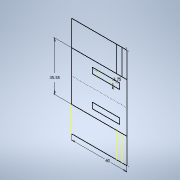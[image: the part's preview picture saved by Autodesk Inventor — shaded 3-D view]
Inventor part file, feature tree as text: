
AUTODESK INVENTOR PART (.ipt)
format: ipt  version: 2022 (Build 260153070, 153G)  size: 130,560 bytes
history: native  units: mm
features: other x7, reference x5, extrude x2, sketch x1, plane x1
ambient origin geometry x8: Origin, YZ Plane, XZ Plane, XY Plane, X Axis, Y Axis, Z Axis, Center Point
bodies: Solid1 (feature_tree)
feature tree (16):
  sketch  "Sketch1"  dims[d1=35.55mm d2=1.0mm d3=3.75mm d4=40.0mm d5=2.75mm d6=0.0mm d7=2.75mm d8=0.0mm]
  extrude  "Extrusion1"  Depth=2.75mm
  plane  "Work Plane1"
  extrude  "Extrusion2"  Depth=2.75mm
  reference  "Reference1"
  reference  "Reference2"
  reference  "Reference4"
  reference  "Reference5"
  reference  "Reference6"
  other  "<userpath> laptop\Desktop\SumoBot\FullBot.iam"
  other  "FullBot.iam"
  other  "MotorEncoderAssembly_MIR:1"
  other  "TT encoder disk_MIR:1"
  other  "MotorEncoderAssembly:1"
  other  "TT motor output:1"
  other  "MotorEncoderBracket:1"
